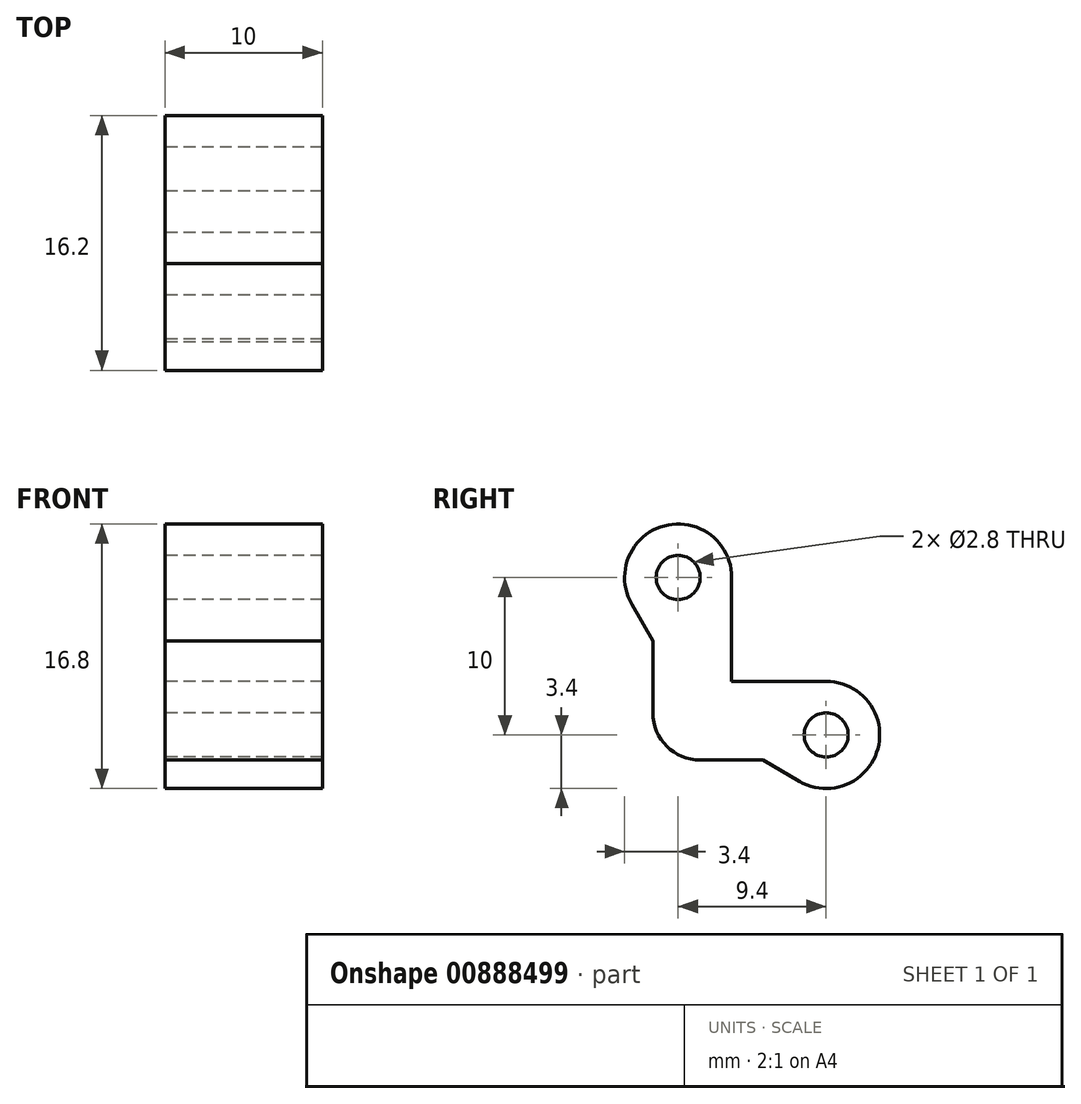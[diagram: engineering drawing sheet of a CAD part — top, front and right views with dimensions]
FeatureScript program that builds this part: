
annotation { "Feature Type Name" : "Feature", "Feature Type Description" : "" }
export const myFeature = defineFeature(function(context is Context, id is Id, definition is map)
    precondition{}
    {
        {
            var Q0;
            Q0=qCreatedBy(makeId("Right.planeOp"),FACE);
            var sketch = newSketch(context, id + "F0", { "sketchPlane" : qUnion([Q0])});
            skCircle(sketch, "E0", {"center": v(0, 0) * mm, "radius": 1.4 * mm});
            skCircle(sketch, "E1", {"center": v(0, 0) * mm, "radius": 3.4 * mm});
            skLineSegment(sketch, "E2", {"start": v(0, 3.4) * mm, "end": v(-6, 3.4) * mm});
            skLineSegment(sketch, "E3", {"start": v(-6, 3.4) * mm, "end": v(-6, 10) * mm});
            skCircle(sketch, "E4", {"center": v(-9.4, 10) * mm, "radius": 1.4 * mm});
            skCircle(sketch, "E5", {"center": v(-9.4, 10) * mm, "radius": 3.4 * mm});
            skLineSegment(sketch, "E6", {"start": v(-11, 5.97) * mm, "end": v(-11, -1.6) * mm});
            skLineSegment(sketch, "E7", {"start": v(-11, -1.6) * mm, "end": v(-4.03, -1.6) * mm});
            skLineSegment(sketch, "E8", {"start": v(-4.03, -1.6) * mm, "end": v(-1.7, -2.94) * mm});
            skLineSegment(sketch, "E9", {"start": v(-11, 5.97) * mm, "end": v(-12.34, 8.3) * mm});
            skLineSegment(sketch, "E10", {"start": v(-6, 3.4) * mm, "end": v(-11, 3.4) * mm, "construction": true});
            skLineSegment(sketch, "E11", {"start": v(-6, 3.4) * mm, "end": v(-6, -1.6) * mm, "construction": true});
            skSolve(sketch);
        }
        {
            var Q0;
            Q0 = qSketchRegion(id + "F0", true);
            extrude(context, id + "F1", {"entities" : qUnion([Q0]), "depth" : 10 * mm, "offsetDistance" : 25 * mm});
        }
        {
            var Q0;
            Q0=makeQuery(id+"F1.opExtrude","SWEPT_EDGE",EDGE,{"disambiguationData":[OSD([sQuery(id+"F0.wireOp",EDGE,"E6"),sQuery(id+"F0.wireOp",EDGE,"E7")])]});
            fillet(context, id + "F2", {"entities" : qUnion([Q0]), "radius" : 3 * mm, "tangentPropagation" : true, "allowEdgeOverflow" : false});
        }
    });
